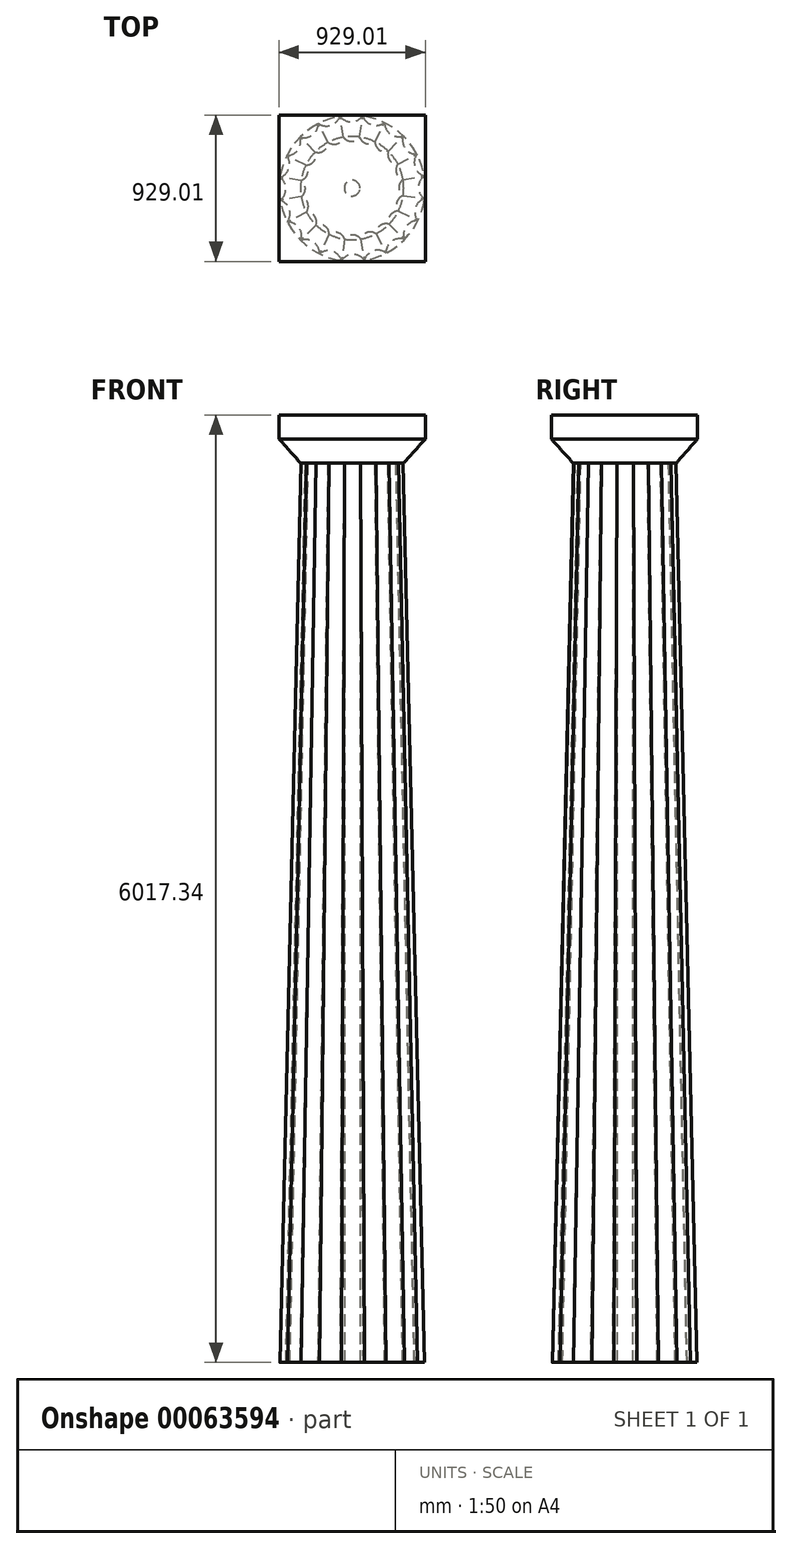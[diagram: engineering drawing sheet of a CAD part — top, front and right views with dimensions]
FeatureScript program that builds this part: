
annotation { "Feature Type Name" : "Feature", "Feature Type Description" : "" }
export const myFeature = defineFeature(function(context is Context, id is Id, definition is map)
    precondition{}
    {
        {
            var Q0;
            Q0=qCreatedBy(makeId("Top.planeOp"),FACE);
            var sketch = newSketch(context, id + "F0", { "sketchPlane" : qUnion([Q0])});
            skCircle(sketch, "E0", {"center": v(-241.8, -595.57) * mm, "radius": 510 * mm});
            skCircle(sketch, "E1", {"center": v(-247.21, -85.6) * mm, "radius": 88.9 * mm});
            skCircle(sketch, "E2.1.0", {"center": v(-404.54, -112.24) * mm, "radius": 88.9 * mm});
            skCircle(sketch, "E2.2.0", {"center": v(-545.93, -186.18) * mm, "radius": 88.9 * mm});
            skCircle(sketch, "E2.3.0", {"center": v(-657.56, -300.2) * mm, "radius": 88.9 * mm});
            skCircle(sketch, "E2.4.0", {"center": v(-728.48, -443.14) * mm, "radius": 88.9 * mm});
            skCircle(sketch, "E2.5.0", {"center": v(-751.77, -601) * mm, "radius": 88.9 * mm});
            skCircle(sketch, "E2.6.0", {"center": v(-725.14, -758.31) * mm, "radius": 88.9 * mm});
            skCircle(sketch, "E2.7.0", {"center": v(-651.2, -899.7) * mm, "radius": 88.9 * mm});
            skCircle(sketch, "E2.8.0", {"center": v(-537.17, -1011.33) * mm, "radius": 88.9 * mm});
            skCircle(sketch, "E2.9.0", {"center": v(-394.24, -1082.26) * mm, "radius": 88.9 * mm});
            skCircle(sketch, "E2.10.0", {"center": v(-236.38, -1105.55) * mm, "radius": 88.9 * mm});
            skCircle(sketch, "E2.11.0", {"center": v(-79.06, -1078.91) * mm, "radius": 88.9 * mm});
            skCircle(sketch, "E2.12.0", {"center": v(62.34, -1004.97) * mm, "radius": 88.9 * mm});
            skCircle(sketch, "E2.13.0", {"center": v(173.96, -890.95) * mm, "radius": 88.9 * mm});
            skCircle(sketch, "E2.14.0", {"center": v(244.89, -748.01) * mm, "radius": 88.9 * mm});
            skCircle(sketch, "E2.15.0", {"center": v(268.17, -590.16) * mm, "radius": 88.9 * mm});
            skCircle(sketch, "E2.16.0", {"center": v(241.54, -432.83) * mm, "radius": 88.9 * mm});
            skCircle(sketch, "E2.17.0", {"center": v(167.6, -291.44) * mm, "radius": 88.9 * mm});
            skCircle(sketch, "E2.18.0", {"center": v(53.57, -179.82) * mm, "radius": 88.9 * mm});
            skCircle(sketch, "E2.19.0", {"center": v(-89.36, -108.89) * mm, "radius": 88.9 * mm});
            skSolve(sketch);
        }
        {
            var Q0;
            {var subQ1=sQuery(id+"F0.wireOp",EDGE,"E0");var subQ47=sQuery(id+"F0.wireOp",EDGE,"E2.16.0");var subQ53=makeQuery(id+"F0.imprint","INTERSECT",VERTEX,{"disambiguationData":[OD(0.0)],"derivedFrom":[subQ1,subQ47]});Q0=makeQuery(id+"F0.imprint","IMPRINT",FACE,{"disambiguationData":[TD([[makeQuery(id+"F0.imprint","IMPRINT",EDGE,{"disambiguationData":[TD([[subQ53,1.0]])],"derivedFrom":subQ1}),1.0]])]});}
            var sketch = newSketch(context, id + "F1", { "sketchPlane" : qUnion([Q0])});
            skCircle(sketch, "E3", {"center": v(-241.8, -595.57) * mm, "radius": 50 * mm});
            skSolve(sketch);
        }
        {
            var Q0;
            Q0=makeQuery(id+"F1.imprint","IMPRINT",FACE,{"disambiguationData":[TD([[makeQuery(id+"F1.imprint","IMPRINT",EDGE,{"derivedFrom":sQuery(id+"F1.wireOp",EDGE,"E3")}),1.0]])]});
            extrude(context, id + "F2", {"entities" : qUnion([Q0]), "depth" : 5710 * mm});
        }
        {
            var Q0;
            Q0=makeQuery(id+"F2.opExtrude","CAP_FACE",FACE,{"disambiguationData":[OSD([sQuery(id+"F1.wireOp",EDGE,"E3")])],"isStart":false});
            cPlane(context, id + "F3", {"entities" : qUnion([Q0]), "cplaneType" : CPlaneType.OFFSET, "offset" : 2.54 * mm, "width" : 152.4 * mm, "height" : 152.4 * mm});
        }
        {
            var Q0;
            Q0=qCreatedBy(id+"F3.planeOp",FACE);
            var sketch = newSketch(context, id + "F4", { "sketchPlane" : qUnion([Q0])});
            skCircle(sketch, "E4", {"center": v(-241.8, -595.57) * mm, "radius": 360 * mm});
            skCircle(sketch, "E5", {"center": v(-245.62, -235.6) * mm, "radius": 62.74 * mm});
            skCircle(sketch, "E6.1.0", {"center": v(-356.67, -254.4) * mm, "radius": 62.74 * mm});
            skCircle(sketch, "E6.2.0", {"center": v(-456.48, -306.6) * mm, "radius": 62.74 * mm});
            skCircle(sketch, "E6.3.0", {"center": v(-535.28, -387.08) * mm, "radius": 62.74 * mm});
            skCircle(sketch, "E6.4.0", {"center": v(-585.34, -487.97) * mm, "radius": 62.74 * mm});
            skCircle(sketch, "E6.5.0", {"center": v(-601.78, -599.4) * mm, "radius": 62.74 * mm});
            skCircle(sketch, "E6.6.0", {"center": v(-582.98, -710.45) * mm, "radius": 62.74 * mm});
            skCircle(sketch, "E6.7.0", {"center": v(-530.78, -810.26) * mm, "radius": 62.74 * mm});
            skCircle(sketch, "E6.8.0", {"center": v(-450.3, -889.05) * mm, "radius": 62.74 * mm});
            skCircle(sketch, "E6.9.0", {"center": v(-349.4, -939.12) * mm, "radius": 62.74 * mm});
            skCircle(sketch, "E6.10.0", {"center": v(-237.98, -955.55) * mm, "radius": 62.74 * mm});
            skCircle(sketch, "E6.11.0", {"center": v(-126.92, -936.75) * mm, "radius": 62.74 * mm});
            skCircle(sketch, "E6.12.0", {"center": v(-27.11, -884.56) * mm, "radius": 62.74 * mm});
            skCircle(sketch, "E6.13.0", {"center": v(51.68, -804.07) * mm, "radius": 62.74 * mm});
            skCircle(sketch, "E6.14.0", {"center": v(101.74, -703.18) * mm, "radius": 62.74 * mm});
            skCircle(sketch, "E6.15.0", {"center": v(118.18, -591.75) * mm, "radius": 62.74 * mm});
            skCircle(sketch, "E6.16.0", {"center": v(99.38, -480.7) * mm, "radius": 62.74 * mm});
            skCircle(sketch, "E6.17.0", {"center": v(47.18, -380.9) * mm, "radius": 62.74 * mm});
            skCircle(sketch, "E6.18.0", {"center": v(-33.3, -302.1) * mm, "radius": 62.74 * mm});
            skCircle(sketch, "E6.19.0", {"center": v(-134.2, -252.03) * mm, "radius": 62.74 * mm});
            skSolve(sketch);
        }
        {
            var Q0;
            {var subQ26=sQuery(id+"F4.wireOp",EDGE,"E6.1.0");var subQ27=sQuery(id+"F4.wireOp",EDGE,"E5");var subQ28=makeQuery(id+"F4.imprint","INTERSECT",VERTEX,{"disambiguationData":[OD(1.0)],"derivedFrom":[subQ27,subQ26]});Q0=makeQuery(id+"F4.imprint","IMPRINT",FACE,{"disambiguationData":[TD([[makeQuery(id+"F4.imprint","IMPRINT",EDGE,{"disambiguationData":[TD([[subQ28,-1.0]])],"derivedFrom":subQ27}),-1.0]])]});}
            var Q1;
            {var subQ20=sQuery(id+"F0.wireOp",EDGE,"E2.1.0");var subQ21=sQuery(id+"F0.wireOp",EDGE,"E1");var subQ22=makeQuery(id+"F0.imprint","INTERSECT",VERTEX,{"disambiguationData":[OD(1.0)],"derivedFrom":[subQ21,subQ20]});Q1=makeQuery(id+"F0.imprint","IMPRINT",FACE,{"disambiguationData":[TD([[makeQuery(id+"F0.imprint","IMPRINT",EDGE,{"disambiguationData":[TD([[subQ22,-1.0]])],"derivedFrom":subQ21}),-1.0]])]});}
            loft(context, id + "F5", {"sheetProfilesArray" : [{ "sheetProfileEntities" : qUnion([Q0]) }, { "sheetProfileEntities" : qUnion([Q1]) }]});
        }
        {
            var Q0;
            Q0=qCreatedBy(id+"F3.planeOp",FACE);
            var sketch = newSketch(context, id + "F6", { "sketchPlane" : qUnion([Q0])});
            skCircle(sketch, "E7", {"center": v(-241.8, -595.57) * mm, "radius": 327.92 * mm});
            skSolve(sketch);
        }
        {
            var Q0;
            Q0=makeQuery(id+"F6.imprint","IMPRINT",FACE,{"disambiguationData":[TD([[makeQuery(id+"F6.imprint","IMPRINT",EDGE,{"derivedFrom":sQuery(id+"F6.wireOp",EDGE,"E7")}),1.0]])]});
            cPlane(context, id + "F7", {"entities" : qUnion([Q0]), "cplaneType" : CPlaneType.OFFSET, "offset" : 152.4 * mm, "width" : 152.4 * mm, "height" : 152.4 * mm});
        }
        {
            var Q0;
            Q0=qCreatedBy(id+"F7.planeOp",FACE);
            var sketch = newSketch(context, id + "F8", { "sketchPlane" : qUnion([Q0])});
            skCircle(sketch, "E8", {"center": v(-241.26, -597.03) * mm, "radius": 464.5 * mm});
            skSolve(sketch);
        }
        {
            var Q1;
            Q1=makeQuery(id+"F8.imprint","IMPRINT",FACE,{"disambiguationData":[TD([[makeQuery(id+"F8.imprint","IMPRINT",EDGE,{"derivedFrom":sQuery(id+"F8.wireOp",EDGE,"E8")}),1.0]])]});
            var Q2;
            Q2=makeQuery(id+"F6.imprint","IMPRINT",FACE,{"disambiguationData":[TD([[makeQuery(id+"F6.imprint","IMPRINT",EDGE,{"derivedFrom":sQuery(id+"F6.wireOp",EDGE,"E7")}),1.0]])]});
            loft(context, id + "F9", {"operationType" : NewBodyOperationType.ADD, "sheetProfilesArray" : [{ "sheetProfileEntities" : qUnion([Q1]) }, { "sheetProfileEntities" : qUnion([Q2]) }]});
        }
        {
            var Q0;
            Q0=qCreatedBy(id+"F7.planeOp",FACE);
            var sketch = newSketch(context, id + "F10", { "sketchPlane" : qUnion([Q0])});
            skLineSegment(sketch, "E9.bottom", {"start": v(-705.76, -132.52) * mm, "end": v(223.25, -132.52) * mm});
            skLineSegment(sketch, "E9.top", {"start": v(-705.76, -1061.53) * mm, "end": v(223.25, -1061.53) * mm});
            skLineSegment(sketch, "E9.left", {"start": v(-705.76, -132.52) * mm, "end": v(-705.76, -1061.53) * mm});
            skLineSegment(sketch, "E9.right", {"start": v(223.25, -132.52) * mm, "end": v(223.25, -1061.53) * mm});
            skSolve(sketch);
        }
        {
            var Q0;
            Q0=makeQuery(id+"F10.imprint","IMPRINT",FACE,{"disambiguationData":[TD([[makeQuery(id+"F10.imprint","IMPRINT",EDGE,{"derivedFrom":sQuery(id+"F10.wireOp",EDGE,"E9.bottom")}),-1.0]])]});
            extrude(context, id + "F11", {"entities" : qUnion([Q0]), "operationType" : NewBodyOperationType.ADD, "depth" : 152.4 * mm});
        }
    });
